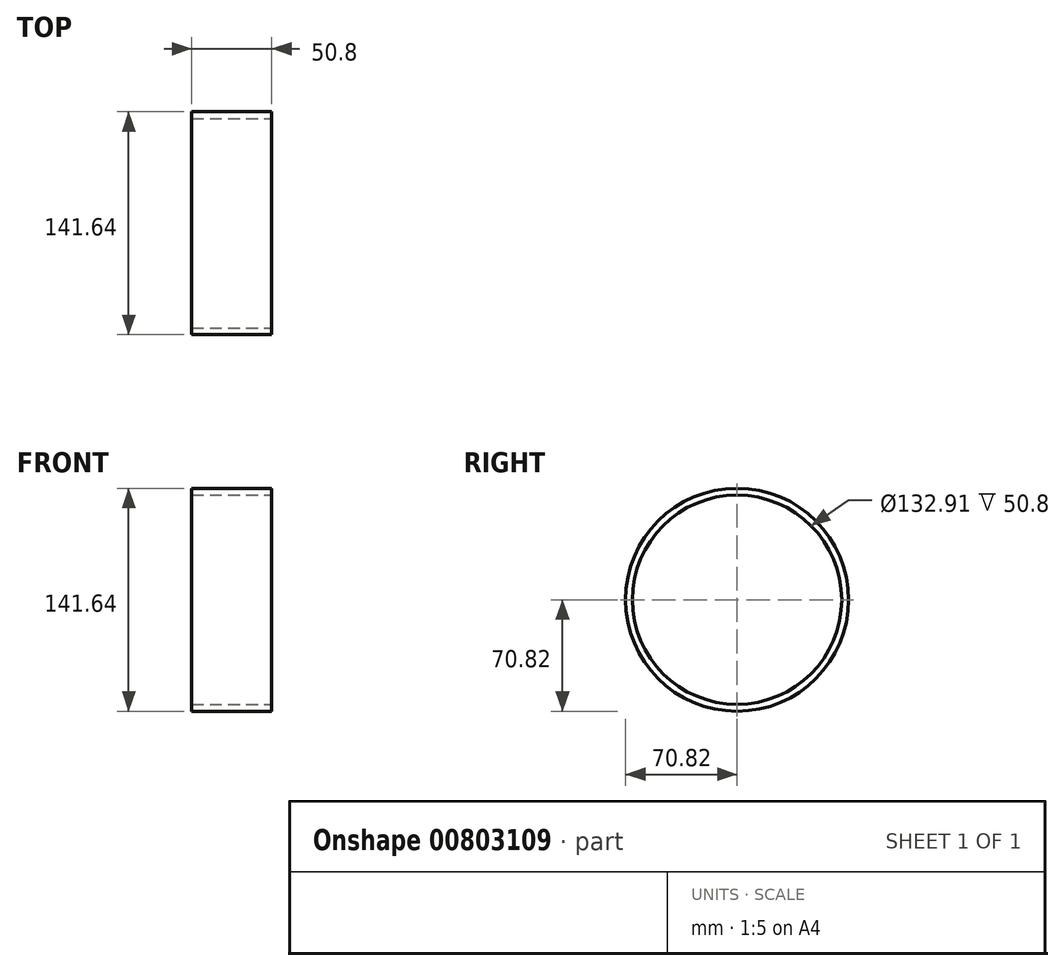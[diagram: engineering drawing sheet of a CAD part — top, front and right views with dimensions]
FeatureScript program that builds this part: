
annotation { "Feature Type Name" : "Feature", "Feature Type Description" : "" }
export const myFeature = defineFeature(function(context is Context, id is Id, definition is map)
    precondition{}
    {
        {
            var Q0;
            Q0=qCreatedBy(makeId("Right.planeOp"),FACE);
            var sketch = newSketch(context, id + "F0", { "sketchPlane" : qUnion([Q0])});
            skCircle(sketch, "E0", {"center": v(0, 0) * mm, "radius": 70.82 * mm});
            skCircle(sketch, "E1", {"center": v(0, 0) * mm, "radius": 61.27 * mm});
            skCircle(sketch, "E2", {"center": v(0, 0) * mm, "radius": 66.46 * mm});
            skSolve(sketch);
        }
        {
            var Q0;
            Q0=makeQuery(id+"F0.imprint","IMPRINT",FACE,{"disambiguationData":[TD([[makeQuery(id+"F0.imprint","IMPRINT",EDGE,{"derivedFrom":sQuery(id+"F0.wireOp",EDGE,"E0")}),1.0]])]});
            extrude(context, id + "F1", {"entities" : qUnion([Q0]), "oppositeDirection" : true, "depth" : 50.8 * mm, "offsetDistance" : 25.4 * mm});
        }
    });
